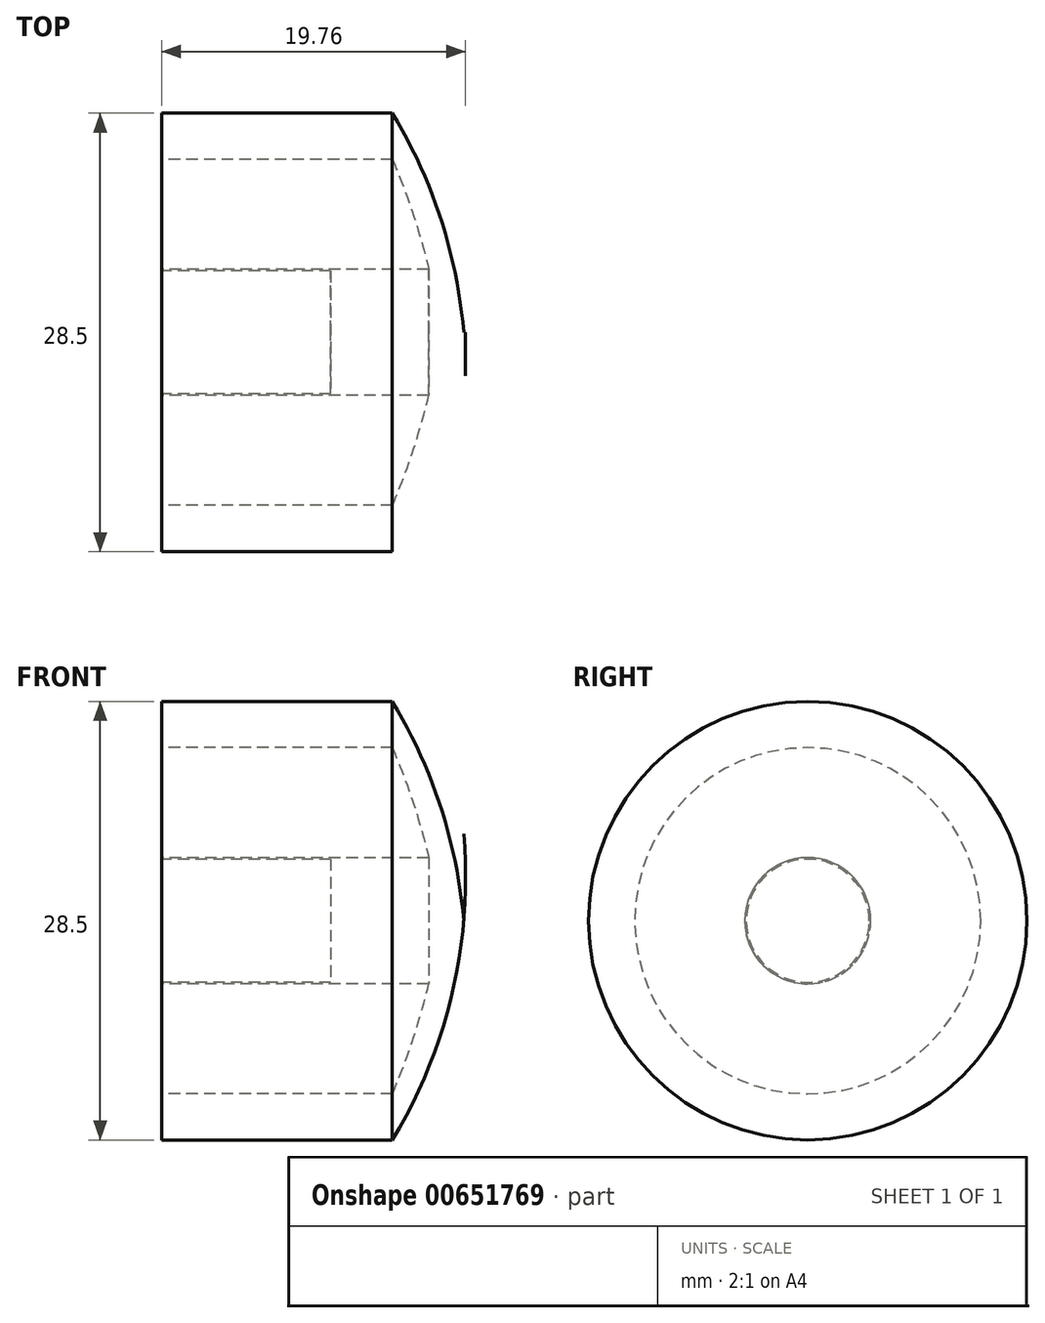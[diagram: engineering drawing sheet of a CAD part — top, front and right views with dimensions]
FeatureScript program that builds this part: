
annotation { "Feature Type Name" : "Feature", "Feature Type Description" : "" }
export const myFeature = defineFeature(function(context is Context, id is Id, definition is map)
    precondition{}
    {
        {
            var Q0;
            Q0=qCreatedBy(makeId("Top.planeOp"),FACE);
            var sketch = newSketch(context, id + "F0", { "sketchPlane" : qUnion([Q0])});
            skLineSegment(sketch, "E0.bottom", {"start": v(0, 14.25) * mm, "end": v(15, 14.25) * mm});
            skLineSegment(sketch, "E0.top", {"start": v(0, 11.25) * mm, "end": v(15, 11.25) * mm});
            skLineSegment(sketch, "E0.left", {"start": v(0, 14.25) * mm, "end": v(0, 11.25) * mm});
            skLineSegment(sketch, "E0.right", {"start": v(15, 14.25) * mm, "end": v(15, 11.25) * mm});
            skLineSegment(sketch, "E1", {"start": v(0, 0) * mm, "end": v(32.04, 0) * mm, "construction": true});
            skLineSegment(sketch, "E2", {"start": v(0, 0) * mm, "end": v(0, 4.44) * mm, "construction": true});
            skArc(sketch, "E3", {"start": v(19.64, 0) * mm, "mid": v(18.14, 7.4) * mm, "end": v(15, 14.25) * mm});
            skArc(sketch, "E4", {"start": v(18.14, 0) * mm, "mid": v(16.94, 5.73) * mm, "end": v(15, 11.25) * mm});
            skLineSegment(sketch, "E5", {"start": v(19.64, 0) * mm, "end": v(18.14, 0) * mm});
            skSolve(sketch);
        }
        {
            var Q0;
            Q0=makeQuery(id+"F0.imprint","IMPRINT",FACE,{"disambiguationData":[TD([[makeQuery(id+"F0.imprint","IMPRINT",EDGE,{"derivedFrom":sQuery(id+"F0.wireOp",EDGE,"E0.bottom")}),-1.0]])]});
            var Q1;
            Q1=makeQuery(id+"F0.imprint","IMPRINT",FACE,{"disambiguationData":[TD([[makeQuery(id+"F0.imprint","IMPRINT",EDGE,{"derivedFrom":sQuery(id+"F0.wireOp",EDGE,"E0.right")}),1.0]])]});
            var Q2;
            Q2=sQuery(id+"F0.wireOp",EDGE,"E1");
            revolve(context, id + "F1", {"entities" : qUnion([Q0, Q1]), "axis" : qUnion([Q2]), "revolveType" : RevolveType.FULL});
        }
        {
            var Q0;
            Q0=qCreatedBy(makeId("Right.planeOp"),FACE);
            var sketch = newSketch(context, id + "F2", { "sketchPlane" : qUnion([Q0])});
            skCircle(sketch, "E6", {"center": v(0, 0) * mm, "radius": 4.1 * mm});
            skSolve(sketch);
        }
        {
            var Q0;
            Q0=makeQuery(id+"F2.imprint","IMPRINT",FACE,{"disambiguationData":[TD([[makeQuery(id+"F2.imprint","IMPRINT",EDGE,{"derivedFrom":sQuery(id+"F2.wireOp",EDGE,"E6")}),1.0]])]});
            extrude(context, id + "F3", {"entities" : qUnion([Q0]), "operationType" : NewBodyOperationType.ADD, "endBound" : BoundingType.UP_TO_NEXT, "depth" : 25 * mm, "offsetDistance" : 25 * mm});
        }
        {
            var Q0;
            Q0=makeQuery(id+"F3.opExtrude","CAP_FACE",FACE,{"disambiguationData":[OSD([sQuery(id+"F2.wireOp",EDGE,"E6")])],"isStart":true});
            var sketch = newSketch(context, id + "F4", { "sketchPlane" : qUnion([Q0])});
            skCircle(sketch, "E7", {"center": v(0, 0) * mm, "radius": 4 * mm});
            skSolve(sketch);
        }
        {
            var Q0;
            Q0=makeQuery(id+"F4.imprint","IMPRINT",FACE,{"disambiguationData":[TD([[makeQuery(id+"F4.imprint","IMPRINT",EDGE,{"derivedFrom":sQuery(id+"F4.wireOp",EDGE,"E7")}),1.0]])]});
            extrude(context, id + "F5", {"entities" : qUnion([Q0]), "operationType" : NewBodyOperationType.REMOVE, "oppositeDirection" : true, "depth" : 11 * mm, "offsetDistance" : 25 * mm});
        }
    });
